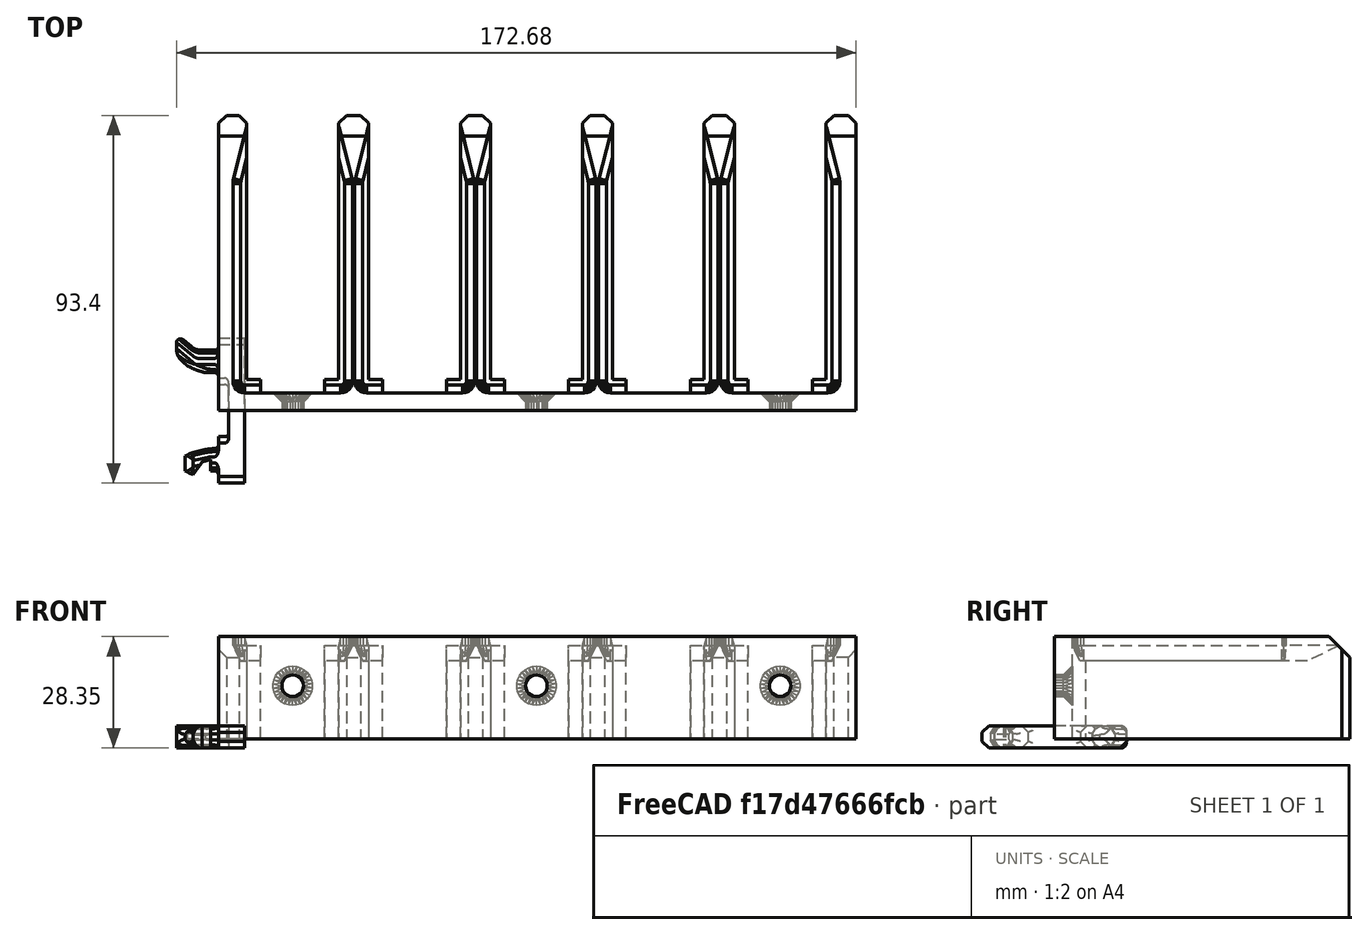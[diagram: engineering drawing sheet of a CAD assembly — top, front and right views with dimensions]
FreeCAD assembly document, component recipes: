
FREECAD ASSEMBLY — COMPONENT RECIPES ("MultiboardMagRack")

This assembly document has 2 components, labeled P0..P1 below (a component is one placed body or linked part). 0 of them carry a construction recipe — the FreeCAD feature program that regenerates the part from scratch, quoted from this document or its linked companion documents; the rest are supplied as boundary geometry only. No exploded tour is included for this assembly.
COMPONENT P0 — geometry summary ("MagRack"; no construction recipe available for this part):
  bounding box: 162.0 x 75.0 x 26.0 mm
  tessellated surface: 1,464 triangles
  volume: 488074610179407585492608085512013516475379831473471420355350790881687680742394572715364273407047761920 mm^3 (154502883880787475082666216583095010719809487627219607524195411663016331706764386219828423054852096% of its bounding box)
COMPONENT P1 — geometry summary ("MultiboardPeg"; no construction recipe available for this part):
  bounding box: 36.8 x 17.3 x 5.7 mm
  tessellated surface: 830 triangles
  volume: 13333333331783160828575141285458323161491547330676364677616111807239181715147782104694183406201733120 mm^3 (367851339926538228446465345656048072045520497392318013939287232856871494959789451848644320645087232% of its bounding box)
  symmetry: mirror-symmetric across its z mid-plane
PROVENANCE & LICENSES
A FreeCAD (.FCStd) document from a public repository crawl; recipes are the document's own serialized feature recipes (and, for linked parts, companion documents' recipes).
License: as declared in the source repository (recorded in the dataset sidecar).
